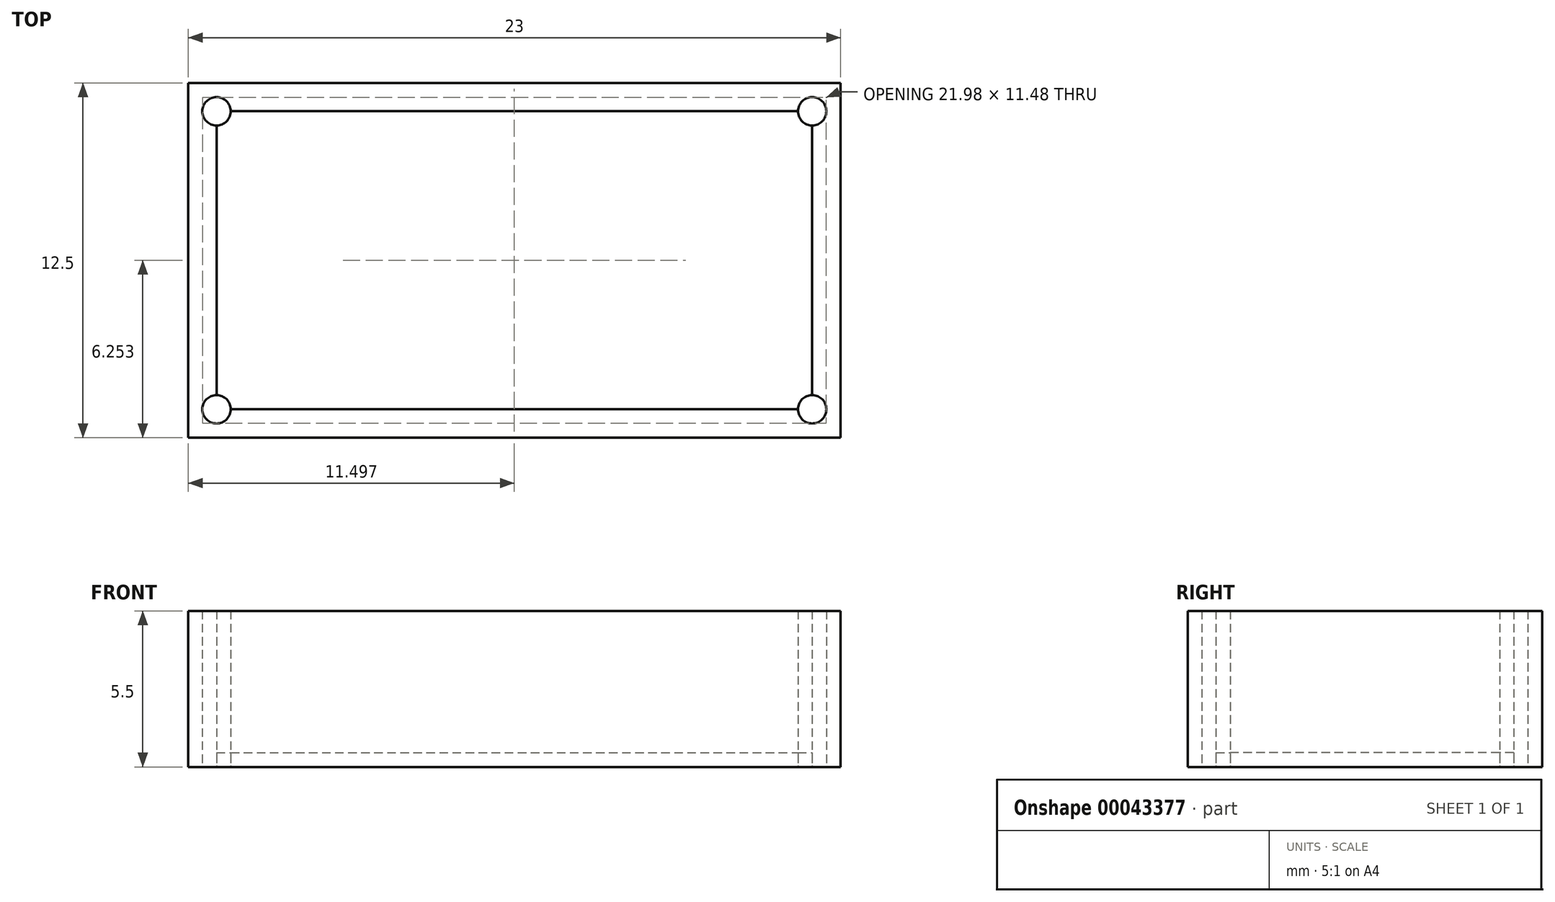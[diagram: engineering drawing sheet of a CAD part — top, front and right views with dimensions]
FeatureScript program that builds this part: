
annotation { "Feature Type Name" : "Feature", "Feature Type Description" : "" }
export const myFeature = defineFeature(function(context is Context, id is Id, definition is map)
    precondition{}
    {
        {
            var Q0;
            Q0=qCreatedBy(makeId("Top.planeOp"),FACE);
            var sketch = newSketch(context, id + "F0", { "sketchPlane" : qUnion([Q0])});
            skLineSegment(sketch, "E0.bottom", {"start": v(-20.16, 3.24) * mm, "end": v(2.84, 3.24) * mm});
            skLineSegment(sketch, "E0.top", {"start": v(-20.16, -9.26) * mm, "end": v(2.84, -9.26) * mm});
            skLineSegment(sketch, "E0.left", {"start": v(-20.16, 3.24) * mm, "end": v(-20.16, -9.26) * mm});
            skLineSegment(sketch, "E0.right", {"start": v(2.84, 3.24) * mm, "end": v(2.84, -9.26) * mm});
            skLineSegment(sketch, "E1.bottom", {"start": v(-19.16, 2.24) * mm, "end": v(1.84, 2.24) * mm});
            skLineSegment(sketch, "E1.top", {"start": v(-19.16, -8.26) * mm, "end": v(1.84, -8.26) * mm});
            skLineSegment(sketch, "E1.left", {"start": v(-19.16, 2.24) * mm, "end": v(-19.16, -8.26) * mm});
            skLineSegment(sketch, "E1.right", {"start": v(1.84, 2.24) * mm, "end": v(1.84, -8.26) * mm});
            skLineSegment(sketch, "E2", {"start": v(2.84, 3.24) * mm, "end": v(1.84, 2.24) * mm, "construction": true});
            skLineSegment(sketch, "E3", {"start": v(-20.16, 3.24) * mm, "end": v(-19.16, 2.24) * mm, "construction": true});
            skLineSegment(sketch, "E4", {"start": v(1.84, -8.26) * mm, "end": v(2.84, -9.26) * mm, "construction": true});
            skLineSegment(sketch, "E5", {"start": v(-20.16, -9.26) * mm, "end": v(-19.16, -8.26) * mm, "construction": true});
            skPoint(sketch, "E6", {"position": v(-19.52, -8.61) * mm});
            skPoint(sketch, "E7", {"position": v(2.2, 2.6) * mm});
            skPoint(sketch, "E8", {"position": v(-19.52, 2.6) * mm});
            skPoint(sketch, "E9", {"position": v(2.2, -8.61) * mm});
            skCircle(sketch, "E10", {"center": v(1.84, 2.24) * mm, "radius": 0.5 * mm});
            skCircle(sketch, "E11", {"center": v(-19.16, 2.24) * mm, "radius": 0.5 * mm});
            skCircle(sketch, "E12", {"center": v(1.84, -8.26) * mm, "radius": 0.5 * mm});
            skCircle(sketch, "E13", {"center": v(-19.16, -8.26) * mm, "radius": 0.5 * mm});
            skSolve(sketch);
        }
        {
            var Q0;
            {var subQ9=sQuery(id+"F0.wireOp",EDGE,"E11");var subQ11=sQuery(id+"F0.wireOp",EDGE,"E1.bottom");var subQ12=makeQuery(id+"F0.imprint","INTERSECT",VERTEX,{"derivedFrom":[subQ11,subQ9]});Q0=makeQuery(id+"F0.imprint","IMPRINT",FACE,{"disambiguationData":[TD([[makeQuery(id+"F0.imprint","IMPRINT",EDGE,{"disambiguationData":[TD([[subQ12,-1.0]])],"derivedFrom":subQ11}),-1.0]])]});}
            extrude(context, id + "F1", {"entities" : qUnion([Q0]), "depth" : 0.5 * mm});
        }
        {
            var Q0;
            Q0=makeQuery(id+"F0.imprint","IMPRINT",FACE,{"disambiguationData":[TD([[makeQuery(id+"F0.imprint","IMPRINT",EDGE,{"derivedFrom":sQuery(id+"F0.wireOp",EDGE,"E0.bottom")}),-1.0]])]});
            extrude(context, id + "F2", {"entities" : qUnion([Q0]), "depth" : 5.5 * mm});
        }
    });
